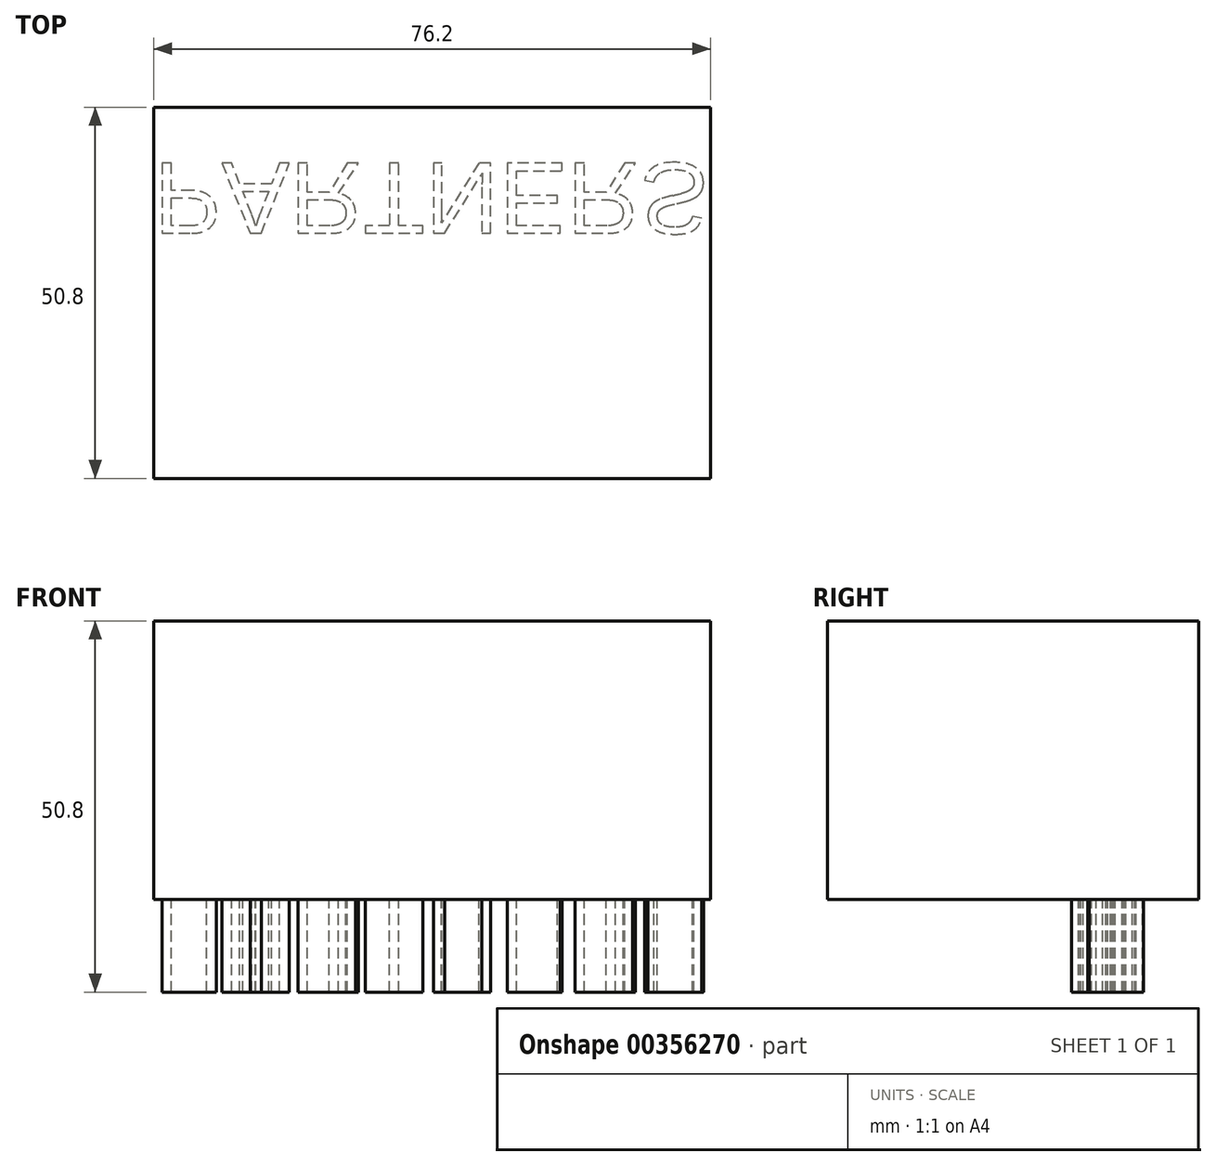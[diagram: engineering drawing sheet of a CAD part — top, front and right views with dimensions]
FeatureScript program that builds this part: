
annotation { "Feature Type Name" : "Feature", "Feature Type Description" : "" }
export const myFeature = defineFeature(function(context is Context, id is Id, definition is map)
    precondition{}
    {
        {
            var Q0;
            Q0=qCreatedBy(makeId("Top.planeOp"),FACE);
            var sketch = newSketch(context, id + "F0", { "sketchPlane" : qUnion([Q0])});
            skLineSegment(sketch, "E0.bottom", {"start": v(-38.1, 25.4) * mm, "end": v(38.1, 25.4) * mm});
            skLineSegment(sketch, "E0.top", {"start": v(-38.1, -25.4) * mm, "end": v(38.1, -25.4) * mm});
            skLineSegment(sketch, "E0.left", {"start": v(-38.1, 25.4) * mm, "end": v(-38.1, -25.4) * mm});
            skLineSegment(sketch, "E0.right", {"start": v(38.1, 25.4) * mm, "end": v(38.1, -25.4) * mm});
            skPoint(sketch, "E0.middle", {"position": v(0, 0) * mm});
            skSolve(sketch);
        }
        {
            var Q0;
            Q0 = qSketchRegion(id + "F0", true);
            extrude(context, id + "F1", {"entities" : qUnion([Q0]), "depth" : 38.1 * mm});
        }
        {
            var Q0;
            Q0=makeQuery(id+"F1.opExtrude","CAP_FACE",FACE,{"disambiguationData":[OSD([sQuery(id+"F0.wireOp",EDGE,"E0.bottom"),sQuery(id+"F0.wireOp",EDGE,"E0.top"),sQuery(id+"F0.wireOp",EDGE,"E0.left"),sQuery(id+"F0.wireOp",EDGE,"E0.right")])],"isStart":true});
            var sketch = newSketch(context, id + "F2", { "sketchPlane" : qUnion([Q0])});
            skText(sketch, "E1", { "text": "PARTNERS", "fontName": "Arimo-Regular.ttf"});
            skLineSegment(sketch, "E2", {"start": v(0, 0) * mm, "end": v(0, -7.68) * mm});
            skLineSegment(sketch, "E3", {"start": v(0, -25.4) * mm, "end": v(0, -17.72) * mm});
            const initialGuessF2  = {"E1": [-0.0381, -0.01772, 1, 0, 0.01003]};
            skSetInitialGuess(sketch, initialGuessF2);
            skSolve(sketch);
        }
        {
            var Q0;
            Q0 = qSketchRegion(id + "F2", true);
            extrude(context, id + "F3", {"entities" : qUnion([Q0]), "operationType" : NewBodyOperationType.ADD, "depth" : 12.7 * mm});
        }
    });
